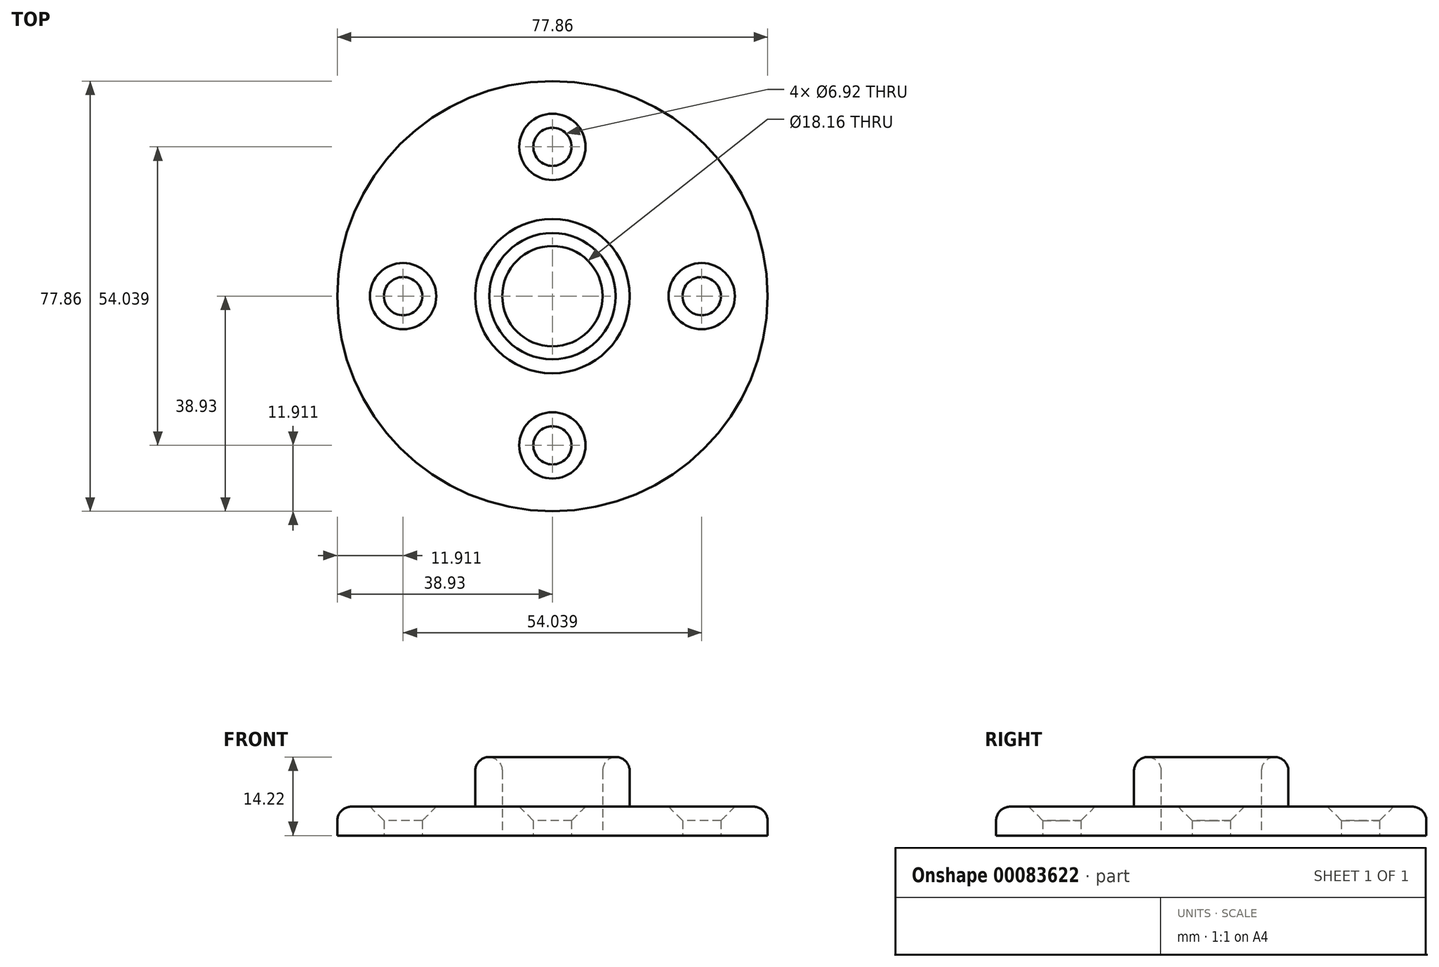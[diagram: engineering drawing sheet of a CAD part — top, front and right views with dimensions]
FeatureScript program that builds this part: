
annotation { "Feature Type Name" : "Feature", "Feature Type Description" : "" }
export const myFeature = defineFeature(function(context is Context, id is Id, definition is map)
    precondition{}
    {
        {
            var Q0;
            Q0=qCreatedBy(makeId("Top.planeOp"),FACE);
            var sketch = newSketch(context, id + "F0", { "sketchPlane" : qUnion([Q0])});
            skCircle(sketch, "E0", {"center": v(0, 0) * mm, "radius": 38.93 * mm});
            skCircle(sketch, "E1", {"center": v(0, 0) * mm, "radius": 13.97 * mm});
            skCircle(sketch, "E2", {"center": v(0, 0) * mm, "radius": 9.08 * mm});
            skCircle(sketch, "E3", {"center": v(0, 27.02) * mm, "radius": 3.46 * mm});
            skCircle(sketch, "E4.1.0", {"center": v(-27.02, 0) * mm, "radius": 3.46 * mm});
            skCircle(sketch, "E4.2.0", {"center": v(0, -27.02) * mm, "radius": 3.46 * mm});
            skCircle(sketch, "E4.3.0", {"center": v(27.02, 0) * mm, "radius": 3.46 * mm});
            skSolve(sketch);
        }
        {
            var Q0;
            Q0=makeQuery(id+"F0.imprint","IMPRINT",FACE,{"disambiguationData":[TD([[makeQuery(id+"F0.imprint","IMPRINT",EDGE,{"derivedFrom":sQuery(id+"F0.wireOp",EDGE,"E0")}),1.0]])]});
            extrude(context, id + "F1", {"entities" : qUnion([Q0]), "depth" : 5.23 * mm});
        }
        {
            var Q0;
            Q0=makeQuery(id+"F0.imprint","IMPRINT",FACE,{"disambiguationData":[TD([[makeQuery(id+"F0.imprint","IMPRINT",EDGE,{"derivedFrom":sQuery(id+"F0.wireOp",EDGE,"E1")}),1.0]])]});
            extrude(context, id + "F2", {"entities" : qUnion([Q0]), "operationType" : NewBodyOperationType.ADD, "depth" : 14.22 * mm});
        }
        {
            var Q0;
            Q0=makeQuery(id+"F1.opExtrude","CAP_EDGE",EDGE,{"disambiguationData":[OSD([sQuery(id+"F0.wireOp",EDGE,"E0")])],"isStart":false});
            var Q1;
            Q1=makeQuery(id+"F2.opExtrude","CAP_EDGE",EDGE,{"disambiguationData":[OSD([sQuery(id+"F0.wireOp",EDGE,"E1")])],"isStart":false});
            var Q2;
            Q2=makeQuery(id+"F1.opExtrude","CAP_EDGE",EDGE,{"disambiguationData":[OSD([sQuery(id+"F0.wireOp",EDGE,"E1")])],"isStart":false});
            fillet(context, id + "F3", {"entities" : qUnion([Q0, Q1, Q2]), "radius" : 2.54 * mm, "tangentPropagation" : true, "allowEdgeOverflow" : false});
        }
        {
            var Q0;
            Q0=makeQuery(id+"F2.opExtrude","CAP_EDGE",EDGE,{"disambiguationData":[OSD([sQuery(id+"F0.wireOp",EDGE,"E2")])],"isStart":false});
            fillet(context, id + "F4", {"entities" : qUnion([Q0]), "radius" : 2.54 * mm, "tangentPropagation" : true, "allowEdgeOverflow" : false});
        }
        {
            var Q0;
            Q0=makeQuery(id+"F1.opExtrude","CAP_EDGE",EDGE,{"disambiguationData":[OSD([sQuery(id+"F0.wireOp",EDGE,"E3")])],"isStart":false});
            var Q1;
            Q1=makeQuery(id+"F1.opExtrude","CAP_EDGE",EDGE,{"disambiguationData":[OSD([sQuery(id+"F0.wireOp",EDGE,"E4.3.0")])],"isStart":false});
            var Q2;
            Q2=makeQuery(id+"F1.opExtrude","CAP_EDGE",EDGE,{"disambiguationData":[OSD([sQuery(id+"F0.wireOp",EDGE,"E4.2.0")])],"isStart":false});
            var Q3;
            Q3=makeQuery(id+"F1.opExtrude","CAP_EDGE",EDGE,{"disambiguationData":[OSD([sQuery(id+"F0.wireOp",EDGE,"E4.1.0")])],"isStart":false});
            chamfer(context, id + "F5", {"entities" : qUnion([Q0, Q1, Q2, Q3]), "width" : 2.54 * mm, "tangentPropagation" : true});
        }
    });
